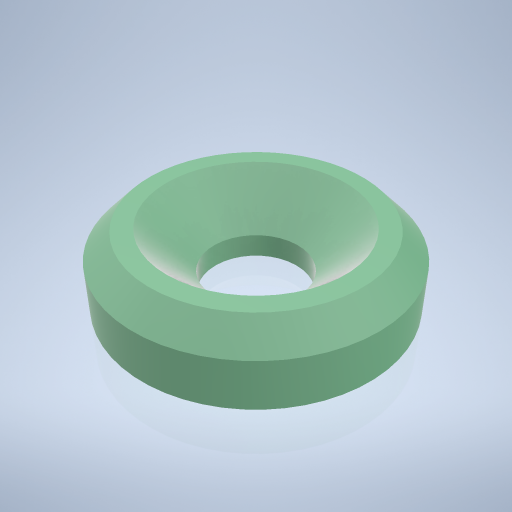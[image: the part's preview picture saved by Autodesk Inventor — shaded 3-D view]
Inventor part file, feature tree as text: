
AUTODESK INVENTOR PART (.ipt)
format: ipt  version: 2024.2 (Build 282272000, 272)  size: 247,808 bytes
history: native  units: mm
features: sketch x2, extrude x1, chamfer x1, hole x1
ambient origin geometry x8: Origin, YZ Plane, XZ Plane, XY Plane, X Axis, Y Axis, Z Axis, Center Point
bodies: Volumenkörper1 (feature_tree)
feature tree (5):
  extrude  "Extrusion1"  Depth=3.0mm TaperAngle=0.0deg
  chamfer  "Fasen1"  Distance=1.0mm Angle=45.0deg
  hole  "Bohrung1"  [1 undecoded]
  sketch  "Skizze1"  dims[d0=12.0mm d1=3.0mm d2=0.0mm d3=1.0mm d4=2.0mm d5=45.0deg]
  sketch  "Skizze2"  dims[d6=4.3mm d7=6.0mm d8=8.4mm d9=2.0mm d10=90.0deg d11=6.0mm d12=0.0mm]
note: 1 required parameter value undecoded (feature->parameter linkage not recoverable at this tier; creation-order binding heuristic only, values carry confidence <= 0.55)
